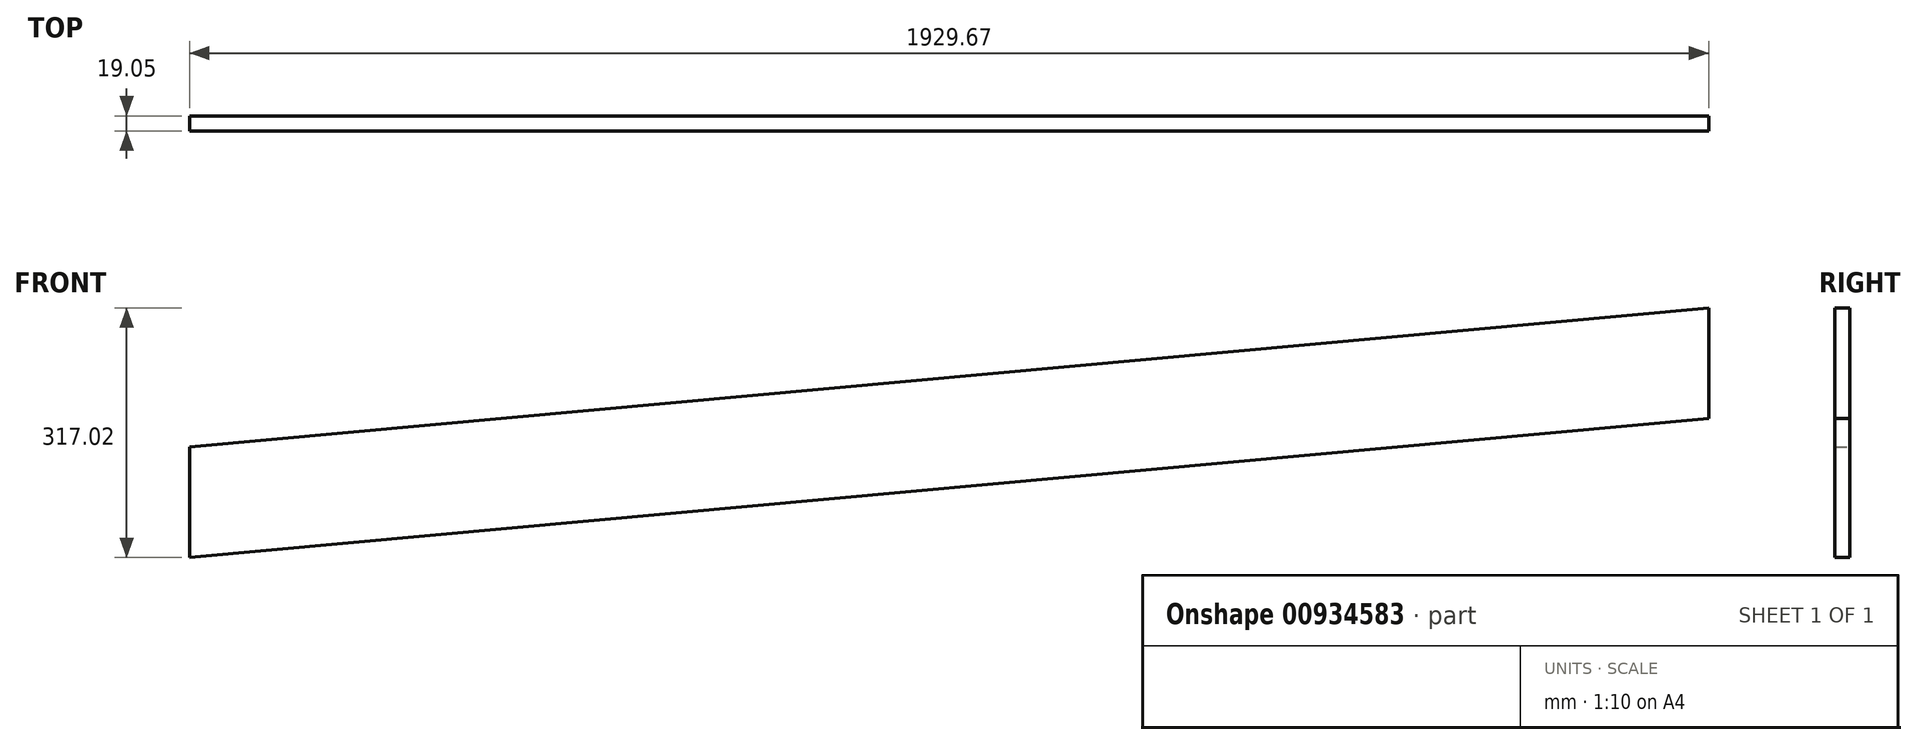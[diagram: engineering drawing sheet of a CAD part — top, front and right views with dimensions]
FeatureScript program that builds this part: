
annotation { "Feature Type Name" : "Feature", "Feature Type Description" : "" }
export const myFeature = defineFeature(function(context is Context, id is Id, definition is map)
    precondition{}
    {
        {
            var Q0;
            Q0=qCreatedBy(makeId("Front.planeOp"),FACE);
            var sketch = newSketch(context, id + "F0", { "sketchPlane" : qUnion([Q0])});
            skLineSegment(sketch, "E0", {"start": v(4228.4, 0) * mm, "end": v(2298.73, -176.74) * mm});
            skLineSegment(sketch, "E1.0", {"start": v(4228.4, -140.28) * mm, "end": v(2298.73, -317.02) * mm});
            skLineSegment(sketch, "E2", {"start": v(2298.73, -176.74) * mm, "end": v(2298.73, -317.02) * mm});
            skLineSegment(sketch, "E3", {"start": v(4228.4, 0) * mm, "end": v(4228.4, -140.28) * mm});
            skSolve(sketch);
        }
        {
            var Q0;
            Q0=makeQuery(id+"F0.imprint","IMPRINT",FACE,{"disambiguationData":[TD([[makeQuery(id+"F0.imprint","IMPRINT",EDGE,{"derivedFrom":sQuery(id+"F0.wireOp",EDGE,"E0")}),1.0]])]});
            extrude(context, id + "F1", {"entities" : qUnion([Q0]), "depth" : 19.05 * mm, "offsetDistance" : 25.4 * mm});
        }
    });
